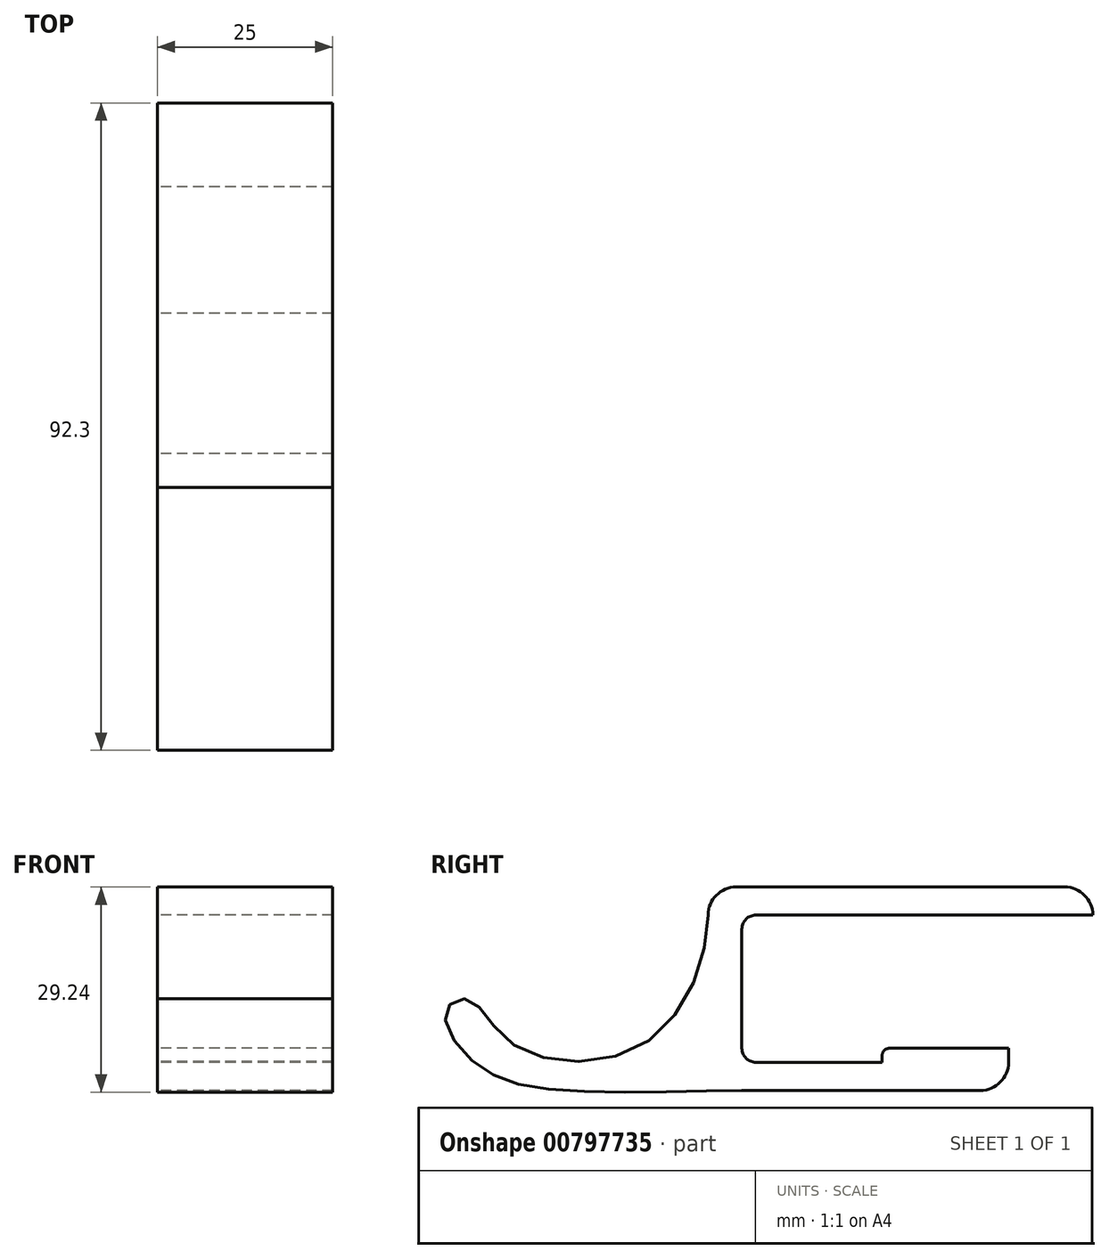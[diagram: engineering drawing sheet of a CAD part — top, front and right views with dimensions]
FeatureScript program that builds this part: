
annotation { "Feature Type Name" : "Feature", "Feature Type Description" : "" }
export const myFeature = defineFeature(function(context is Context, id is Id, definition is map)
    precondition{}
    {
        {
            var Q0;
            Q0=qCreatedBy(makeId("Right.planeOp"),FACE);
            var sketch = newSketch(context, id + "F0", { "sketchPlane" : qUnion([Q0])});
            skLineSegment(sketch, "E0", {"start": v(38, 0) * mm, "end": v(0, 0) * mm});
            skLineSegment(sketch, "E1", {"start": v(0, 0) * mm, "end": v(0, 21) * mm});
            skLineSegment(sketch, "E2", {"start": v(0, 21) * mm, "end": v(50, 21) * mm});
            skFitSpline(sketch, "E3", {"points": [v(-4.81, 21) * mm, v(-13.56, 2.9) * mm, v(-32.6, 2.55) * mm, v(-39, 8.97) * mm, v(-42.2, 7.27) * mm, v(-38.16, 0) * mm, v(-25.53, -4) * mm, v(0, -4) * mm], "startDerivative": vector(0, -99.81) * mm, "endDerivative": vector(104.67, 0) * mm});
            skLineSegment(sketch, "E4", {"start": v(0, -4) * mm, "end": v(38, -4) * mm});
            skLineSegment(sketch, "E5", {"start": v(38, -4) * mm, "end": v(38, 0) * mm});
            skLineSegment(sketch, "E6", {"start": v(50, 21) * mm, "end": v(50, 25) * mm});
            skLineSegment(sketch, "E7", {"start": v(50, 25) * mm, "end": v(-4.81, 25) * mm});
            skLineSegment(sketch, "E8", {"start": v(-4.81, 25) * mm, "end": v(-4.81, 21) * mm});
            skSolve(sketch);
        }
        {
            var Q0;
            Q0=makeQuery(id+"F0.imprint","IMPRINT",FACE,{"disambiguationData":[TD([[makeQuery(id+"F0.imprint","IMPRINT",EDGE,{"derivedFrom":sQuery(id+"F0.wireOp",EDGE,"E0")}),1.0]])]});
            extrude(context, id + "F1", {"entities" : qUnion([Q0]), "depth" : 25 * mm, "offsetDistance" : 25 * mm});
        }
        {
            var Q0;
            Q0=makeQuery(id+"F1.opExtrude","SWEPT_EDGE",EDGE,{"disambiguationData":[OSD([sQuery(id+"F0.wireOp",EDGE,"E7"),sQuery(id+"F0.wireOp",EDGE,"E8")])]});
            var Q1;
            Q1=makeQuery(id+"F1.opExtrude","SWEPT_EDGE",EDGE,{"disambiguationData":[OSD([sQuery(id+"F0.wireOp",EDGE,"E6"),sQuery(id+"F0.wireOp",EDGE,"E7")])]});
            var Q2;
            Q2=makeQuery(id+"F1.opExtrude","SWEPT_EDGE",EDGE,{"disambiguationData":[OSD([sQuery(id+"F0.wireOp",EDGE,"E4"),sQuery(id+"F0.wireOp",EDGE,"E5")])]});
            fillet(context, id + "F2", {"entities" : qUnion([Q0, Q1, Q2]), "radius" : 4 * mm, "tangentPropagation" : true, "allowEdgeOverflow" : false});
        }
        {
            var Q0;
            Q0=makeQuery(id+"F1.opExtrude","SWEPT_EDGE",EDGE,{"disambiguationData":[OSD([sQuery(id+"F0.wireOp",EDGE,"E1"),sQuery(id+"F0.wireOp",EDGE,"E2")])]});
            var Q1;
            Q1=makeQuery(id+"F1.opExtrude","SWEPT_EDGE",EDGE,{"disambiguationData":[OSD([sQuery(id+"F0.wireOp",EDGE,"E0"),sQuery(id+"F0.wireOp",EDGE,"E1")])]});
            fillet(context, id + "F3", {"entities" : qUnion([Q0, Q1]), "radius" : 2 * mm, "tangentPropagation" : true, "allowEdgeOverflow" : false});
        }
        {
            var Q0;
            Q0=makeQuery(id+"F1.opExtrude","SWEPT_FACE",FACE,{"disambiguationData":[OSD([sQuery(id+"F0.wireOp",EDGE,"E0")])]});
            var sketch = newSketch(context, id + "F4", { "sketchPlane" : qUnion([Q0])});
            skLineSegment(sketch, "E9", {"start": v(25, 20) * mm, "end": v(0, 20) * mm});
            skLineSegment(sketch, "E10", {"start": v(0, 20) * mm, "end": v(0, 38) * mm});
            skLineSegment(sketch, "E11", {"start": v(0, 38) * mm, "end": v(25, 38) * mm});
            skLineSegment(sketch, "E12", {"start": v(25, 38) * mm, "end": v(25, 20) * mm});
            skSolve(sketch);
        }
        {
            var Q0;
            Q0=makeQuery(id+"F4.imprint","IMPRINT",FACE,{"disambiguationData":[TD([[makeQuery(id+"F4.imprint","IMPRINT",EDGE,{"derivedFrom":sQuery(id+"F4.wireOp",EDGE,"E9")}),-1.0]])]});
            extrude(context, id + "F5", {"entities" : qUnion([Q0]), "operationType" : NewBodyOperationType.ADD, "depth" : 2 * mm, "offsetDistance" : 25 * mm});
        }
        {
            var Q0;
            Q0=makeQuery(id+"F5.opExtrude","CAP_EDGE",EDGE,{"disambiguationData":[OSD([sQuery(id+"F4.wireOp",EDGE,"E9")])],"isStart":true});
            var Q1;
            Q1=makeQuery(id+"F5.opExtrude","CAP_EDGE",EDGE,{"disambiguationData":[OSD([sQuery(id+"F4.wireOp",EDGE,"E9")])],"isStart":false});
            fillet(context, id + "F6", {"entities" : qUnion([Q0, Q1]), "radius" : 1 * mm, "tangentPropagation" : true, "allowEdgeOverflow" : false});
        }
    });
